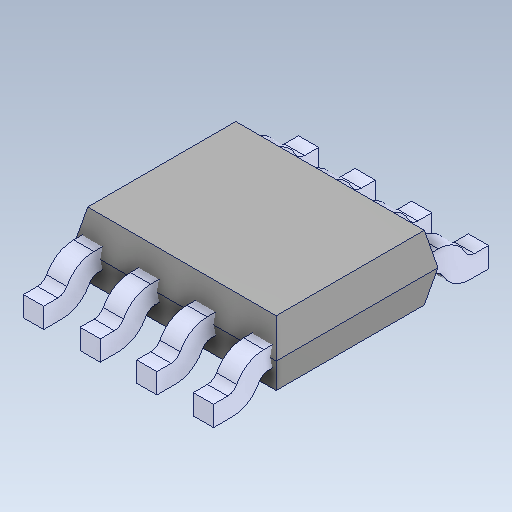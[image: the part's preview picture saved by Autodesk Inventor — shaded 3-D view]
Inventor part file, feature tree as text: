
AUTODESK INVENTOR PART (.ipt)
format: ipt  version: 2020 (Build 240168000, 168)  size: 181,760 bytes
history: native  units: in
note: dims shown in document units (in); Inventor stores cm internally (conversion verified against a paired STEP export)
features: other x4, mirror x4, fillet x1
ambient origin geometry x8: Origin, YZ Plane, XZ Plane, XY Plane, X Axis, Y Axis, Z Axis, Center Point
bodies: Solid1 (feature_tree), Solid2 (feature_tree), Solid3 (feature_tree), Solid4 (feature_tree), Solid5 (feature_tree), Solid6 (feature_tree), Solid7 (feature_tree), Solid8 (feature_tree), Solid9 (feature_tree)
feature tree (9):
  other  "Boss-Extrude1"
  fillet  "Fillet2"  [1 undecoded]
  other  "LPattern2[1]"
  other  "LPattern2[2]"
  other  "LPattern2[3]"
  mirror  "Mirror2[1]"
  mirror  "Mirror2[2]"
  mirror  "Mirror2[3]"
  mirror  "Mirror2[4]"
note: 1 required parameter value undecoded (feature->parameter linkage not recoverable at this tier; creation-order binding heuristic only, values carry confidence <= 0.55)
